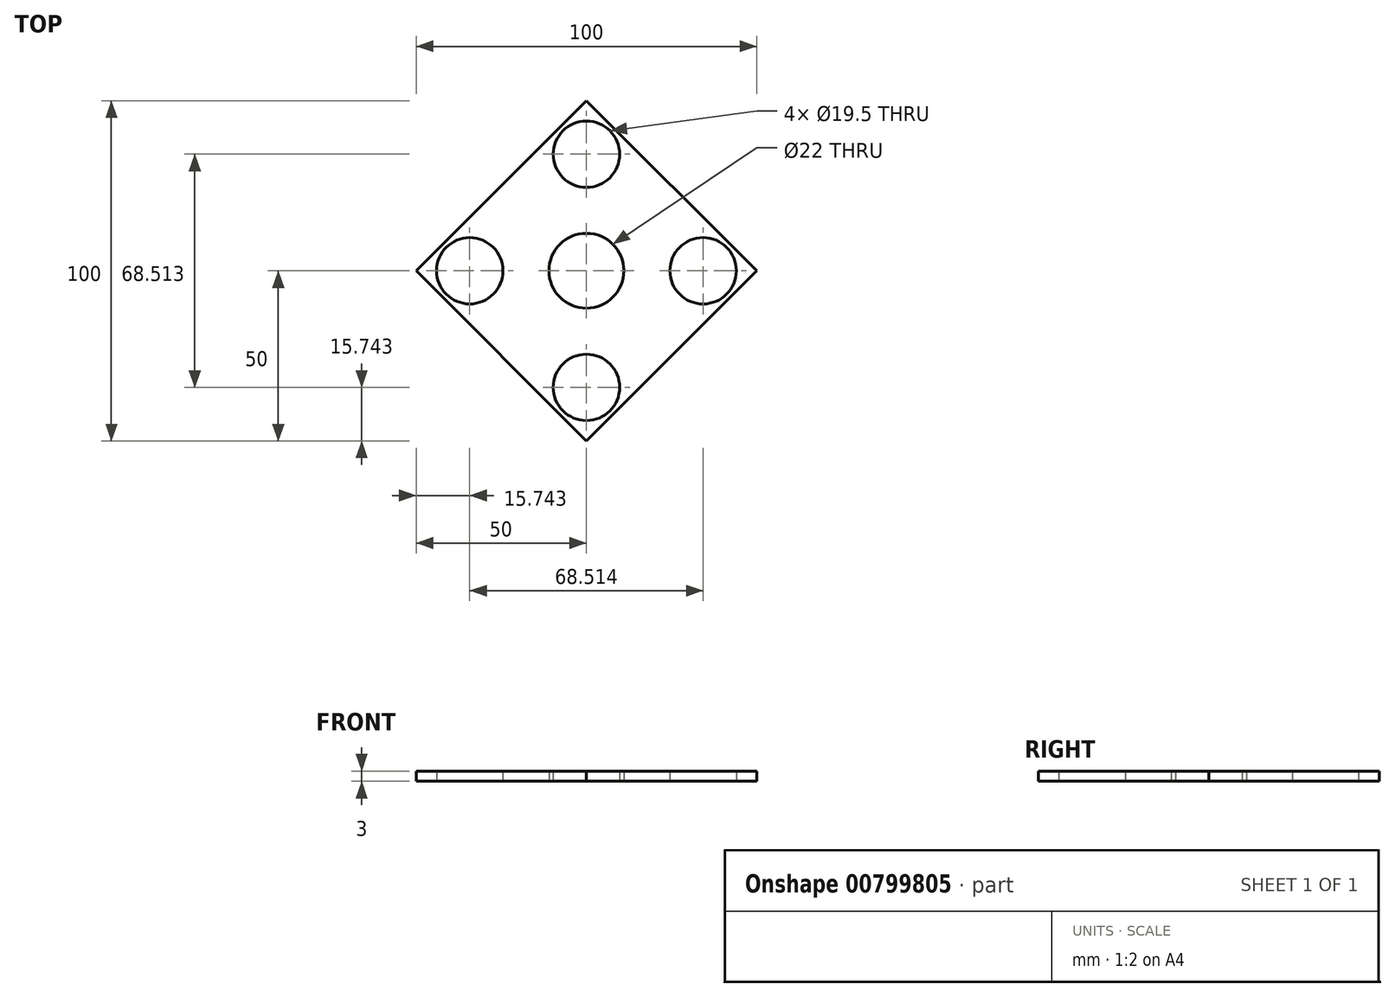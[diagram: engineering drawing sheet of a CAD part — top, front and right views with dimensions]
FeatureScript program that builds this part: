
annotation { "Feature Type Name" : "Feature", "Feature Type Description" : "" }
export const myFeature = defineFeature(function(context is Context, id is Id, definition is map)
    precondition{}
    {
        {
            var Q0;
            Q0=qCreatedBy(makeId("Top.planeOp"),FACE);
            var sketch = newSketch(context, id + "F0", { "sketchPlane" : qUnion([Q0])});
            skCircle(sketch, "E0", {"center": v(0, 0) * mm, "radius": 11 * mm});
            skCircle(sketch, "E1", {"center": v(0, 34.26) * mm, "radius": 9.75 * mm});
            skLineSegment(sketch, "E2", {"start": v(0, 50) * mm, "end": v(-50, 0) * mm});
            skLineSegment(sketch, "E3", {"start": v(0, 50) * mm, "end": v(50, 0) * mm});
            skLineSegment(sketch, "E4.1.0", {"start": v(0, -50) * mm, "end": v(-50, 0) * mm});
            skCircle(sketch, "E4.1.1", {"center": v(0, -34.26) * mm, "radius": 9.75 * mm});
            skLineSegment(sketch, "E4.1.3", {"start": v(0, -50) * mm, "end": v(50, 0) * mm});
            skCircle(sketch, "E5", {"center": v(-34.26, 0) * mm, "radius": 9.75 * mm});
            skCircle(sketch, "E6", {"center": v(34.26, 0) * mm, "radius": 9.75 * mm});
            skSolve(sketch);
        }
        {
            var Q0;
            Q0=makeQuery(id+"F0.imprint","IMPRINT",FACE,{"disambiguationData":[TD([[makeQuery(id+"F0.imprint","IMPRINT",EDGE,{"derivedFrom":sQuery(id+"F0.wireOp",EDGE,"E1")}),-1.0]])]});
            extrude(context, id + "F1", {"entities" : qUnion([Q0]), "depth" : 3 * mm, "offsetDistance" : 25 * mm});
        }
    });
